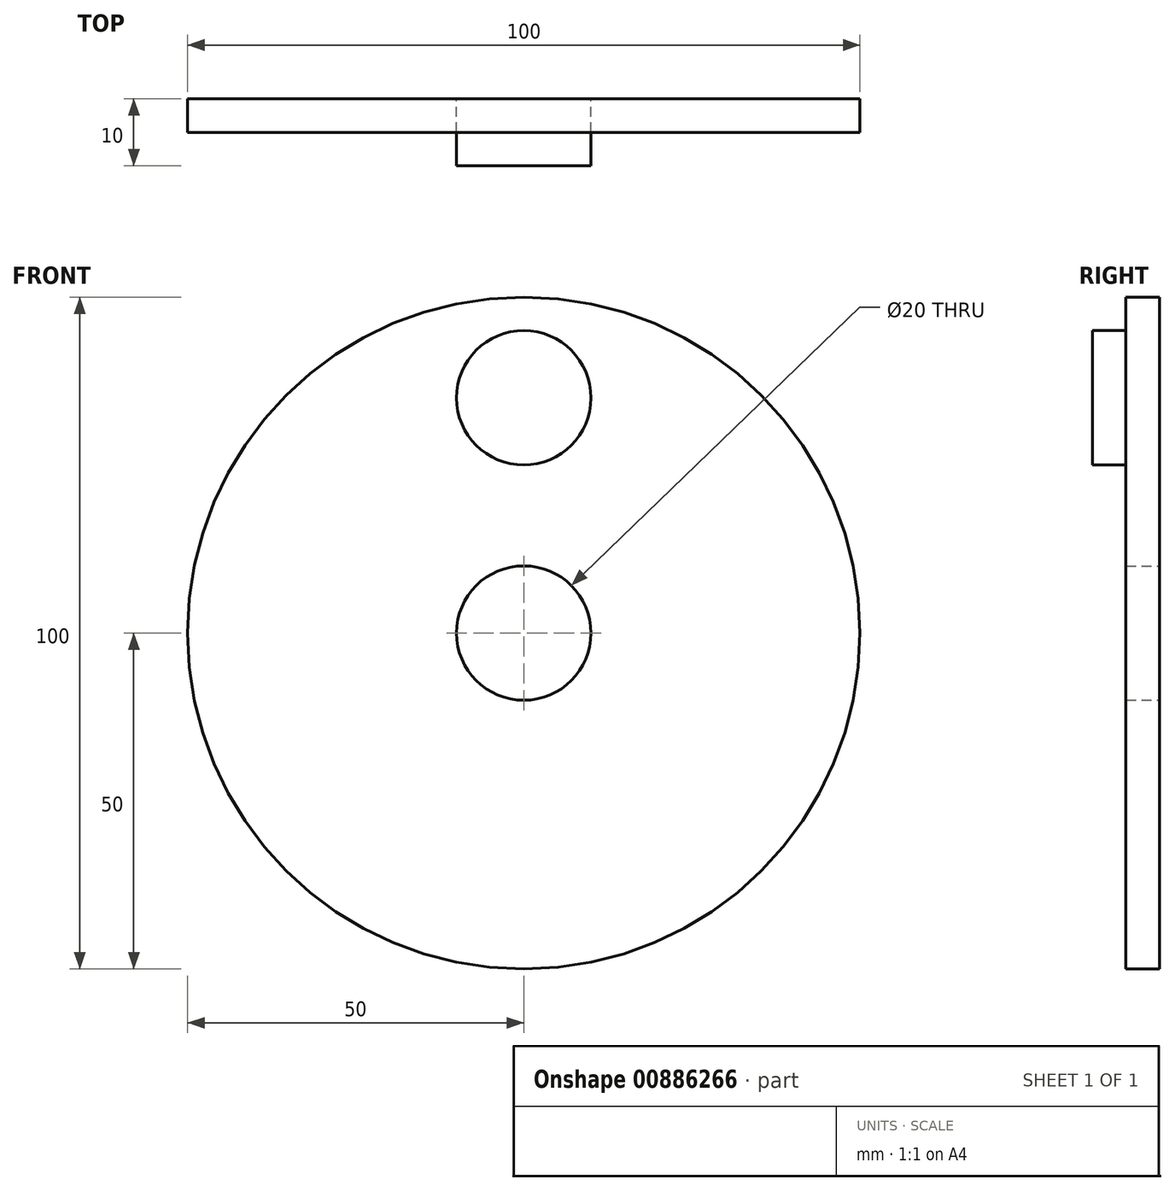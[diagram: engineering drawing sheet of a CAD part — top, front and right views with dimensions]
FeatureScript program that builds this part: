
annotation { "Feature Type Name" : "Feature", "Feature Type Description" : "" }
export const myFeature = defineFeature(function(context is Context, id is Id, definition is map)
    precondition{}
    {
        {
            var Q0;
            Q0=qCreatedBy(makeId("Front.planeOp"),FACE);
            var sketch = newSketch(context, id + "F0", { "sketchPlane" : qUnion([Q0])});
            skCircle(sketch, "E0", {"center": v(0, 0) * mm, "radius": 50 * mm});
            skCircle(sketch, "E1", {"center": v(0, 0) * mm, "radius": 10 * mm});
            skSolve(sketch);
        }
        {
            var Q0;
            Q0 = qSketchRegion(id + "F0", true);
            extrude(context, id + "F1", {"entities" : qUnion([Q0]), "depth" : 5 * mm, "offsetDistance" : 25 * mm, "symmetric" : true});
        }
        {
            var Q0;
            Q0=qCreatedBy(makeId("Front.planeOp"),FACE);
            var sketch = newSketch(context, id + "F2", { "sketchPlane" : qUnion([Q0])});
            skCircle(sketch, "E2", {"center": v(0, 35) * mm, "radius": 10 * mm});
            skSolve(sketch);
        }
        {
            var Q0;
            Q0 = qSketchRegion(id + "F2", true);
            extrude(context, id + "F3", {"entities" : qUnion([Q0]), "operationType" : NewBodyOperationType.ADD, "depth" : 7.5 * mm, "offsetDistance" : 25 * mm});
        }
    });
